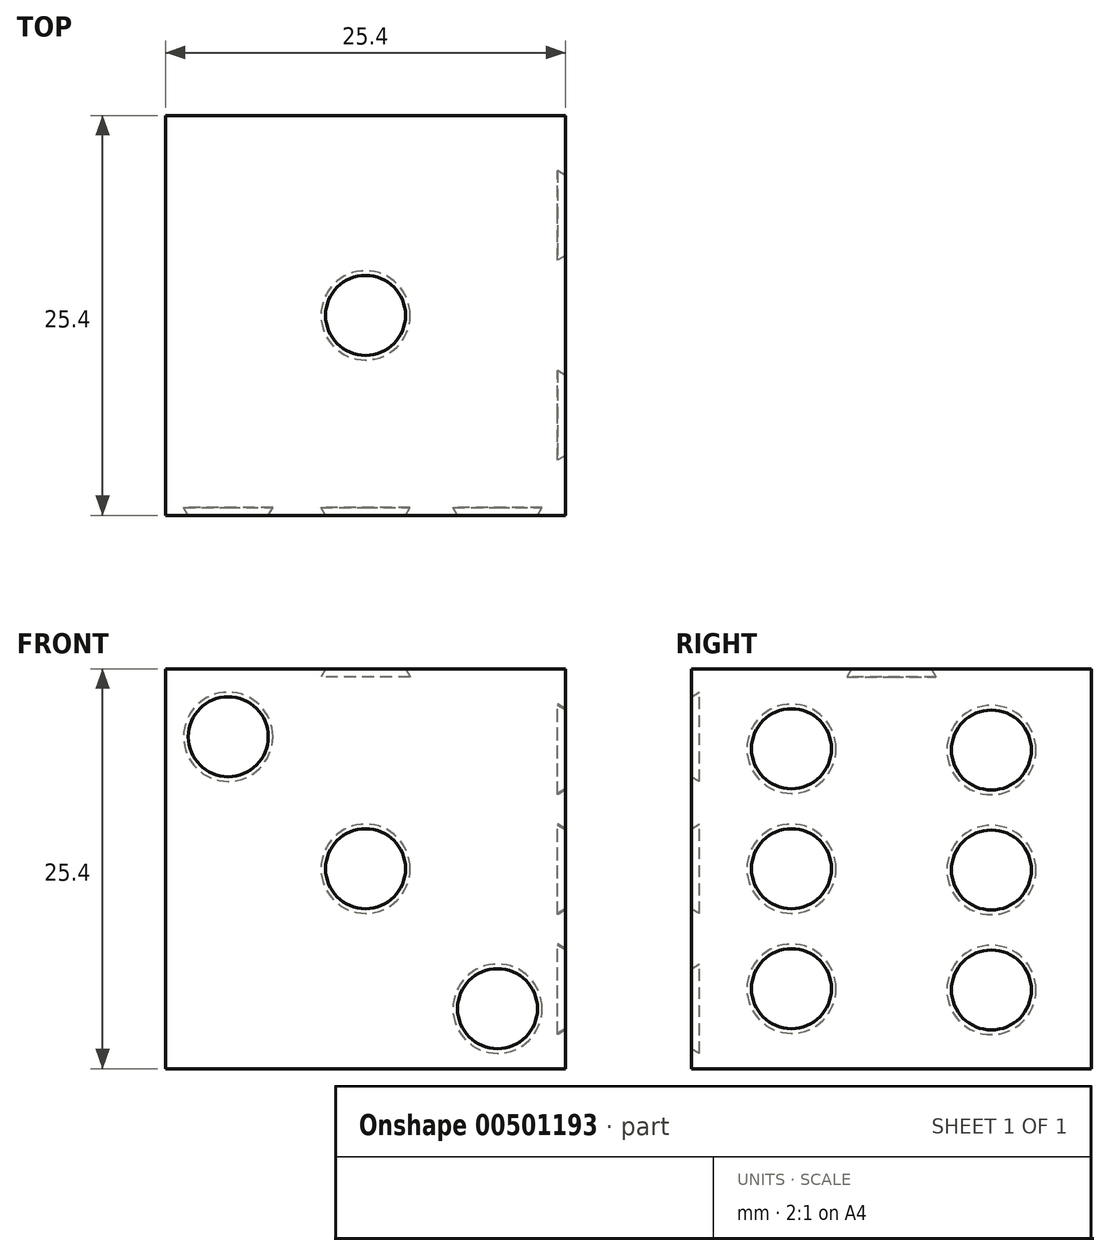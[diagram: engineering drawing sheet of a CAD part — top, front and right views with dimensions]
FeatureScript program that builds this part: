
annotation { "Feature Type Name" : "Feature", "Feature Type Description" : "" }
export const myFeature = defineFeature(function(context is Context, id is Id, definition is map)
    precondition{}
    {
        {
            var Q0;
            Q0=qCreatedBy(makeId("Front.planeOp"),FACE);
            var sketch = newSketch(context, id + "F0", { "sketchPlane" : qUnion([Q0])});
            skLineSegment(sketch, "E0.bottom", {"start": v(-12.7, 12.7) * mm, "end": v(12.7, 12.7) * mm});
            skLineSegment(sketch, "E0.top", {"start": v(-12.7, -12.7) * mm, "end": v(12.7, -12.7) * mm});
            skLineSegment(sketch, "E0.left", {"start": v(-12.7, 12.7) * mm, "end": v(-12.7, -12.7) * mm});
            skLineSegment(sketch, "E0.right", {"start": v(12.7, 12.7) * mm, "end": v(12.7, -12.7) * mm});
            skPoint(sketch, "E0.middle", {"position": v(0, 0) * mm});
            skSolve(sketch);
        }
        {
            var Q0;
            Q0 = qSketchRegion(id + "F0", true);
            extrude(context, id + "F1", {"entities" : qUnion([Q0]), "depth" : 25.4 * mm});
        }
        {
            var Q0;
            Q0=makeQuery(id+"F1.opExtrude","SWEPT_FACE",FACE,{"disambiguationData":[OSD([sQuery(id+"F0.wireOp",EDGE,"E0.bottom")])]});
            var sketch = newSketch(context, id + "F2", { "sketchPlane" : qUnion([Q0])});
            skCircle(sketch, "E1", {"center": v(0, -12.7) * mm, "radius": 2.54 * mm});
            skSolve(sketch);
        }
        {
            var Q0;
            Q0=makeQuery(id+"F2.imprint","IMPRINT",FACE,{"disambiguationData":[TD([[makeQuery(id+"F2.imprint","IMPRINT",EDGE,{"derivedFrom":sQuery(id+"F2.wireOp",EDGE,"E1")}),1.0]])]});
            extrude(context, id + "F3", {"entities" : qUnion([Q0]), "operationType" : NewBodyOperationType.REMOVE, "oppositeDirection" : true, "depth" : 0.5 * mm, "hasDraft" : true, "draftAngle" : 30 * degree});
        }
        {
            var Q0;
            Q0=makeQuery(id+"F1.opExtrude","CAP_FACE",FACE,{"disambiguationData":[OSD([sQuery(id+"F0.wireOp",EDGE,"E0.bottom"),sQuery(id+"F0.wireOp",EDGE,"E0.top"),sQuery(id+"F0.wireOp",EDGE,"E0.left"),sQuery(id+"F0.wireOp",EDGE,"E0.right")])],"isStart":false});
            var sketch = newSketch(context, id + "F4", { "sketchPlane" : qUnion([Q0])});
            skCircle(sketch, "E2", {"center": v(0, 0) * mm, "radius": 2.54 * mm});
            skCircle(sketch, "E3", {"center": v(8.38, -8.9) * mm, "radius": 2.54 * mm});
            skCircle(sketch, "E4", {"center": v(-8.72, 8.38) * mm, "radius": 2.54 * mm});
            skSolve(sketch);
        }
        {
            var Q0;
            Q0=makeQuery(id+"F4.imprint","IMPRINT",FACE,{"disambiguationData":[TD([[makeQuery(id+"F4.imprint","IMPRINT",EDGE,{"derivedFrom":sQuery(id+"F4.wireOp",EDGE,"E4")}),1.0]])]});
            var Q1;
            Q1=makeQuery(id+"F4.imprint","IMPRINT",FACE,{"disambiguationData":[TD([[makeQuery(id+"F4.imprint","IMPRINT",EDGE,{"derivedFrom":sQuery(id+"F4.wireOp",EDGE,"E2")}),1.0]])]});
            var Q2;
            Q2=makeQuery(id+"F4.imprint","IMPRINT",FACE,{"disambiguationData":[TD([[makeQuery(id+"F4.imprint","IMPRINT",EDGE,{"derivedFrom":sQuery(id+"F4.wireOp",EDGE,"E3")}),1.0]])]});
            extrude(context, id + "F5", {"entities" : qUnion([Q0, Q1, Q2]), "operationType" : NewBodyOperationType.REMOVE, "oppositeDirection" : true, "depth" : 0.5 * mm, "hasDraft" : true, "draftAngle" : 30 * degree});
        }
        {
            var Q0;
            Q0=makeQuery(id+"F1.opExtrude","SWEPT_FACE",FACE,{"disambiguationData":[OSD([sQuery(id+"F0.wireOp",EDGE,"E0.right")])]});
            var sketch = newSketch(context, id + "F6", { "sketchPlane" : qUnion([Q0])});
            skCircle(sketch, "E5", {"center": v(-19.05, 7.62) * mm, "radius": 2.54 * mm});
            skCircle(sketch, "E6", {"center": v(-19.05, 0) * mm, "radius": 2.54 * mm});
            skCircle(sketch, "E7", {"center": v(-19.05, -7.62) * mm, "radius": 2.54 * mm});
            skCircle(sketch, "E8", {"center": v(-6.35, 7.54) * mm, "radius": 2.54 * mm});
            skCircle(sketch, "E9", {"center": v(-6.35, -0.08) * mm, "radius": 2.54 * mm});
            skCircle(sketch, "E10", {"center": v(-6.35, -7.7) * mm, "radius": 2.54 * mm});
            skSolve(sketch);
        }
        {
            var Q0;
            Q0=makeQuery(id+"F6.imprint","IMPRINT",FACE,{"disambiguationData":[TD([[makeQuery(id+"F6.imprint","IMPRINT",EDGE,{"derivedFrom":sQuery(id+"F6.wireOp",EDGE,"E8")}),1.0]])]});
            var Q1;
            Q1=makeQuery(id+"F6.imprint","IMPRINT",FACE,{"disambiguationData":[TD([[makeQuery(id+"F6.imprint","IMPRINT",EDGE,{"derivedFrom":sQuery(id+"F6.wireOp",EDGE,"E9")}),1.0]])]});
            var Q2;
            Q2=makeQuery(id+"F6.imprint","IMPRINT",FACE,{"disambiguationData":[TD([[makeQuery(id+"F6.imprint","IMPRINT",EDGE,{"derivedFrom":sQuery(id+"F6.wireOp",EDGE,"E10")}),1.0]])]});
            var Q3;
            Q3=makeQuery(id+"F6.imprint","IMPRINT",FACE,{"disambiguationData":[TD([[makeQuery(id+"F6.imprint","IMPRINT",EDGE,{"derivedFrom":sQuery(id+"F6.wireOp",EDGE,"E6")}),1.0]])]});
            var Q4;
            Q4=makeQuery(id+"F6.imprint","IMPRINT",FACE,{"disambiguationData":[TD([[makeQuery(id+"F6.imprint","IMPRINT",EDGE,{"derivedFrom":sQuery(id+"F6.wireOp",EDGE,"E5")}),1.0]])]});
            var Q5;
            Q5=makeQuery(id+"F6.imprint","IMPRINT",FACE,{"disambiguationData":[TD([[makeQuery(id+"F6.imprint","IMPRINT",EDGE,{"derivedFrom":sQuery(id+"F6.wireOp",EDGE,"E7")}),1.0]])]});
            extrude(context, id + "F7", {"entities" : qUnion([Q0, Q1, Q2, Q3, Q4, Q5]), "operationType" : NewBodyOperationType.REMOVE, "oppositeDirection" : true, "depth" : 0.5 * mm, "hasDraft" : true, "draftAngle" : 30 * degree});
        }
    });
